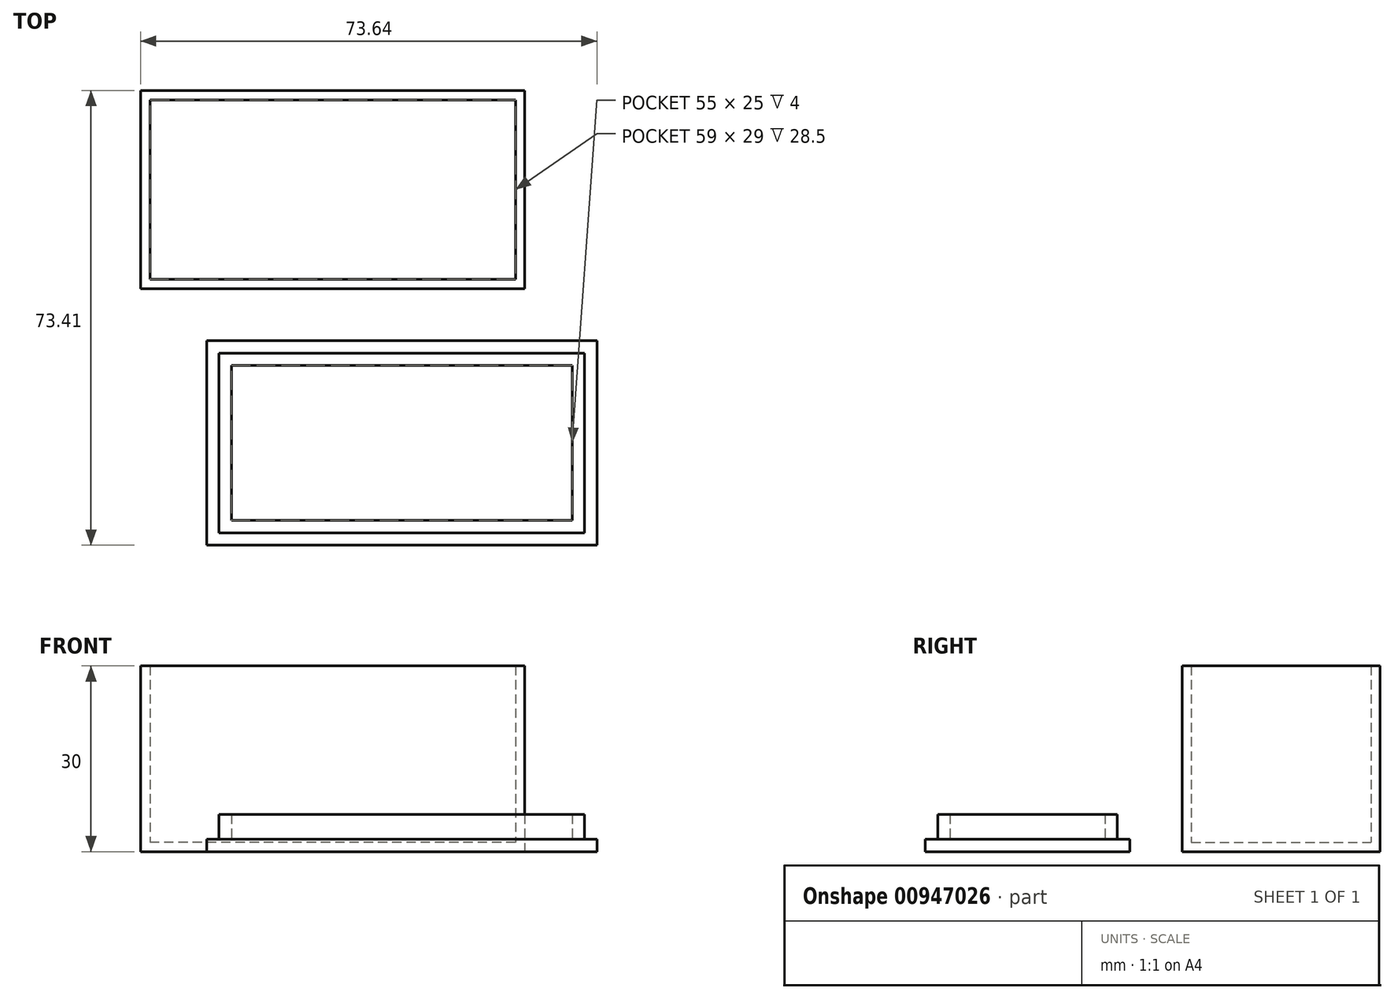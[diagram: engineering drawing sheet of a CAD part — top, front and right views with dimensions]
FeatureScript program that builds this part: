
annotation { "Feature Type Name" : "Feature", "Feature Type Description" : "" }
export const myFeature = defineFeature(function(context is Context, id is Id, definition is map)
    precondition{}
    {
        {
            var Q0;
            Q0=qCreatedBy(makeId("Top.planeOp"),FACE);
            var sketch = newSketch(context, id + "F0", { "sketchPlane" : qUnion([Q0])});
            skLineSegment(sketch, "E0.bottom", {"start": v(4.56, -1.12) * mm, "end": v(-57.44, -1.12) * mm});
            skLineSegment(sketch, "E0.top", {"start": v(4.56, 30.88) * mm, "end": v(-57.44, 30.88) * mm});
            skLineSegment(sketch, "E0.left", {"start": v(4.56, -1.12) * mm, "end": v(4.56, 30.88) * mm});
            skLineSegment(sketch, "E0.right", {"start": v(-57.44, -1.12) * mm, "end": v(-57.44, 30.88) * mm});
            skPoint(sketch, "E0.middle", {"position": v(-26.44, 14.88) * mm});
            skSolve(sketch);
        }
        {
            var Q0;
            Q0 = qSketchRegion(id + "F0", true);
            extrude(context, id + "F1", {"entities" : qUnion([Q0]), "depth" : 30 * mm, "offsetDistance" : 25 * mm});
        }
        {
            var Q0;
            Q0=makeQuery(id+"F1.opExtrude","CAP_FACE",FACE,{"disambiguationData":[OSD([sQuery(id+"F0.wireOp",EDGE,"E0.bottom"),sQuery(id+"F0.wireOp",EDGE,"E0.top"),sQuery(id+"F0.wireOp",EDGE,"E0.left"),sQuery(id+"F0.wireOp",EDGE,"E0.right")])],"isStart":false});
            shell(context, id + "F2", {"entities" : qUnion([Q0]), "thickness" : 1.5 * mm});
        }
        {
            var Q0;
            Q0=qCreatedBy(makeId("Top.planeOp"),FACE);
            var sketch = newSketch(context, id + "F3", { "sketchPlane" : qUnion([Q0])});
            skLineSegment(sketch, "E1.bottom", {"start": v(-46.8, -42.53) * mm, "end": v(16.2, -42.53) * mm});
            skLineSegment(sketch, "E1.top", {"start": v(-46.8, -9.53) * mm, "end": v(16.2, -9.53) * mm});
            skLineSegment(sketch, "E1.left", {"start": v(-46.8, -42.53) * mm, "end": v(-46.8, -9.53) * mm});
            skLineSegment(sketch, "E1.right", {"start": v(16.2, -42.53) * mm, "end": v(16.2, -9.53) * mm});
            skPoint(sketch, "E1.middle", {"position": v(-15.3, -26.03) * mm});
            skLineSegment(sketch, "E2.bottom", {"start": v(-44.8, -11.53) * mm, "end": v(14.2, -11.53) * mm});
            skLineSegment(sketch, "E2.top", {"start": v(-44.8, -40.53) * mm, "end": v(14.2, -40.53) * mm});
            skLineSegment(sketch, "E2.left", {"start": v(-44.8, -11.53) * mm, "end": v(-44.8, -40.53) * mm});
            skLineSegment(sketch, "E2.right", {"start": v(14.2, -11.53) * mm, "end": v(14.2, -40.53) * mm});
            skLineSegment(sketch, "E3.bottom", {"start": v(-42.8, -13.53) * mm, "end": v(12.2, -13.53) * mm});
            skLineSegment(sketch, "E3.top", {"start": v(-42.8, -38.53) * mm, "end": v(12.2, -38.53) * mm});
            skLineSegment(sketch, "E3.left", {"start": v(-42.8, -13.53) * mm, "end": v(-42.8, -38.53) * mm});
            skLineSegment(sketch, "E3.right", {"start": v(12.2, -13.53) * mm, "end": v(12.2, -38.53) * mm});
            skSolve(sketch);
        }
        {
            var Q0;
            Q0=makeQuery(id+"F3.imprint","IMPRINT",FACE,{"disambiguationData":[TD([[makeQuery(id+"F3.imprint","IMPRINT",EDGE,{"derivedFrom":sQuery(id+"F3.wireOp",EDGE,"E2.bottom")}),-1.0]])]});
            extrude(context, id + "F4", {"entities" : qUnion([Q0]), "depth" : 4 * mm, "offsetDistance" : 25 * mm});
        }
        {
            var Q0;
            Q0=makeQuery(id+"F3.imprint","IMPRINT",FACE,{"disambiguationData":[TD([[makeQuery(id+"F3.imprint","IMPRINT",EDGE,{"derivedFrom":sQuery(id+"F3.wireOp",EDGE,"E1.bottom")}),1.0]])]});
            var Q1;
            Q1=makeQuery(id+"F3.imprint","IMPRINT",FACE,{"disambiguationData":[TD([[makeQuery(id+"F3.imprint","IMPRINT",EDGE,{"derivedFrom":sQuery(id+"F3.wireOp",EDGE,"E2.bottom")}),-1.0]])]});
            var Q2;
            Q2=makeQuery(id+"F3.imprint","IMPRINT",FACE,{"disambiguationData":[TD([[makeQuery(id+"F3.imprint","IMPRINT",EDGE,{"derivedFrom":sQuery(id+"F3.wireOp",EDGE,"E3.bottom")}),-1.0]])]});
            var Q3;
            Q3=makeQuery(id+"F4.opExtrude","CAP_FACE",FACE,{"disambiguationData":[OSD([sQuery(id+"F3.wireOp",EDGE,"E2.bottom"),sQuery(id+"F3.wireOp",EDGE,"E2.top"),sQuery(id+"F3.wireOp",EDGE,"E2.left"),sQuery(id+"F3.wireOp",EDGE,"E2.right"),sQuery(id+"F3.wireOp",EDGE,"E3.bottom"),sQuery(id+"F3.wireOp",EDGE,"E3.top"),sQuery(id+"F3.wireOp",EDGE,"E3.left"),sQuery(id+"F3.wireOp",EDGE,"E3.right")])],"isStart":false});
            extrude(context, id + "F5", {"entities" : qUnion([Q0, Q1, Q2, Q3]), "operationType" : NewBodyOperationType.ADD, "depth" : 2 * mm, "offsetDistance" : 25 * mm});
        }
    });
